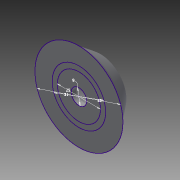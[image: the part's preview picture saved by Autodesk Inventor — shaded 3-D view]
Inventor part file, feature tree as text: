
AUTODESK INVENTOR PART (.ipt)
format: ipt  version: 2014 SP2 (Build 180246200, 246)  size: 108,544 bytes
history: native  units: mm
features: extrude x2, chamfer x2, sketch x1, fillet x1
ambient origin geometry x8: Origin, YZ Plane, XZ Plane, XY Plane, X Axis, Y Axis, Z Axis, Center Point
bodies: Solid1 (feature_tree)
feature tree (6):
  sketch  "Sketch1"  dims[d0=25.0mm d1=31.0mm d2=51.0mm d3=9.0mm d4=3.0mm d5=0.0mm d6=3.0mm d7=2.0mm d8=45.0deg d9=13.0mm d10=0.0mm d11=7.0mm d12=9.0mm d13=45.0deg d14=2.0mm]
  extrude  "Extrusion1"  Depth=2.0mm
  chamfer  "Chamfer1"  Distance=51.0mm
  extrude  "Extrusion2"  Depth=2.0mm
  chamfer  "Chamfer2"  Distance=3.0mm
  fillet  "Fillet1"  Radius=3.0mm
